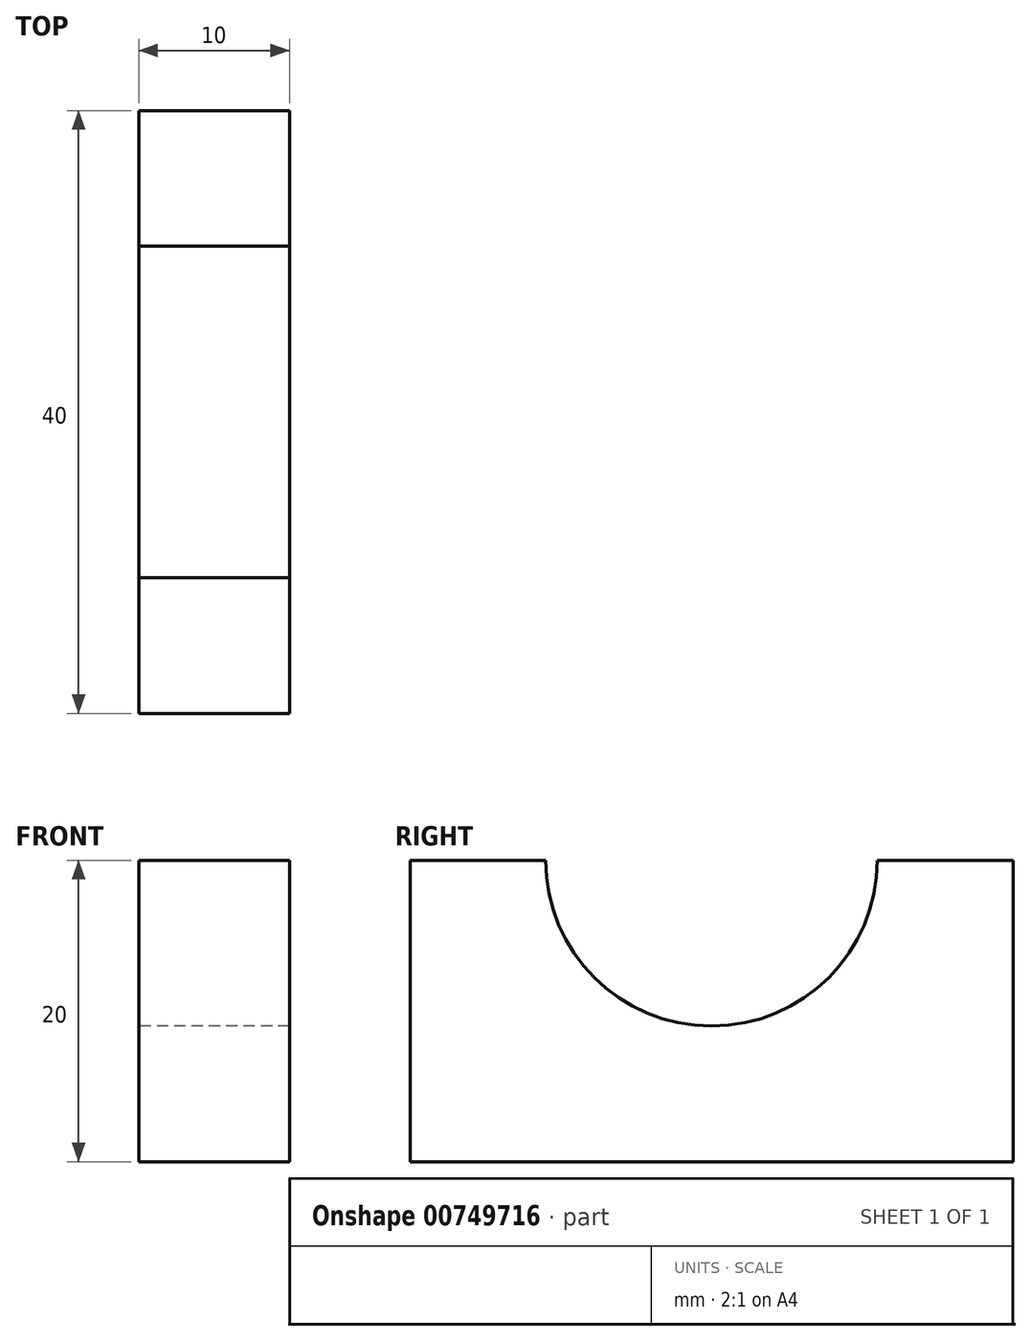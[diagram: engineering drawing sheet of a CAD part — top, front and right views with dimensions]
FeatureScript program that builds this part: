
annotation { "Feature Type Name" : "Feature", "Feature Type Description" : "" }
export const myFeature = defineFeature(function(context is Context, id is Id, definition is map)
    precondition{}
    {
        {
            var Q0;
            Q0=qCreatedBy(makeId("Top.planeOp"),FACE);
            var sketch = newSketch(context, id + "F0", { "sketchPlane" : qUnion([Q0])});
            skLineSegment(sketch, "E0.bottom", {"start": v(-5, 20) * mm, "end": v(5, 20) * mm});
            skLineSegment(sketch, "E0.top", {"start": v(-5, -20) * mm, "end": v(5, -20) * mm});
            skLineSegment(sketch, "E0.left", {"start": v(-5, 20) * mm, "end": v(-5, -20) * mm});
            skLineSegment(sketch, "E0.right", {"start": v(5, 20) * mm, "end": v(5, -20) * mm});
            skPoint(sketch, "E0.middle", {"position": v(0, 0) * mm});
            skSolve(sketch);
        }
        {
            var Q0;
            Q0 = qSketchRegion(id + "F0", true);
            extrude(context, id + "F1", {"entities" : qUnion([Q0]), "depth" : 20 * mm, "offsetDistance" : 25 * mm});
        }
        {
            var Q0;
            Q0=makeQuery(id+"F1.opExtrude","SWEPT_FACE",FACE,{"disambiguationData":[OSD([sQuery(id+"F0.wireOp",EDGE,"E0.left")])]});
            var sketch = newSketch(context, id + "F2", { "sketchPlane" : qUnion([Q0])});
            skCircle(sketch, "E1", {"center": v(0, 20) * mm, "radius": 11 * mm});
            skSolve(sketch);
        }
        {
            var Q0;
            Q0 = qSketchRegion(id + "F2", true);
            extrude(context, id + "F3", {"entities" : qUnion([Q0]), "operationType" : NewBodyOperationType.REMOVE, "endBound" : BoundingType.THROUGH_ALL, "oppositeDirection" : true, "depth" : 25 * mm, "offsetDistance" : 25 * mm});
        }
    });
